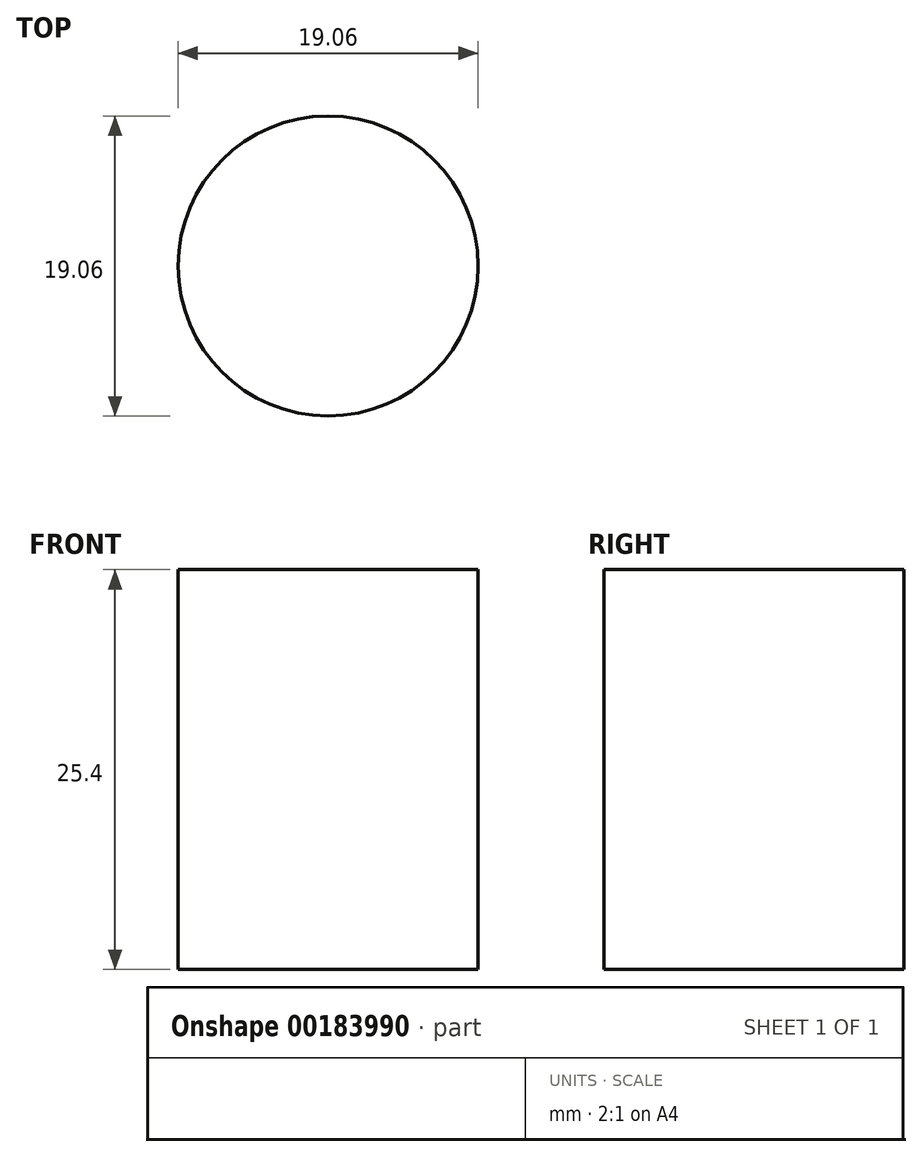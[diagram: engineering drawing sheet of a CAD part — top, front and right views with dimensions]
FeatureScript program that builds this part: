
annotation { "Feature Type Name" : "Feature", "Feature Type Description" : "" }
export const myFeature = defineFeature(function(context is Context, id is Id, definition is map)
    precondition{}
    {
        {
            var Q0;
            Q0=qCreatedBy(makeId("Top.planeOp"),FACE);
            var sketch = newSketch(context, id + "F0", { "sketchPlane" : qUnion([Q0])});
            skCircle(sketch, "E0", {"center": v(0, 0) * mm, "radius": 9.53 * mm});
            skSolve(sketch);
        }
        {
            var Q0;
            Q0=makeQuery(id+"F0.imprint","IMPRINT",FACE,{"disambiguationData":[TD([[makeQuery(id+"F0.imprint","IMPRINT",EDGE,{"derivedFrom":sQuery(id+"F0.wireOp",EDGE,"E0")}),1.0]])]});
            extrude(context, id + "F1", {"entities" : qUnion([Q0]), "depth" : 25.4 * mm});
        }
    });
